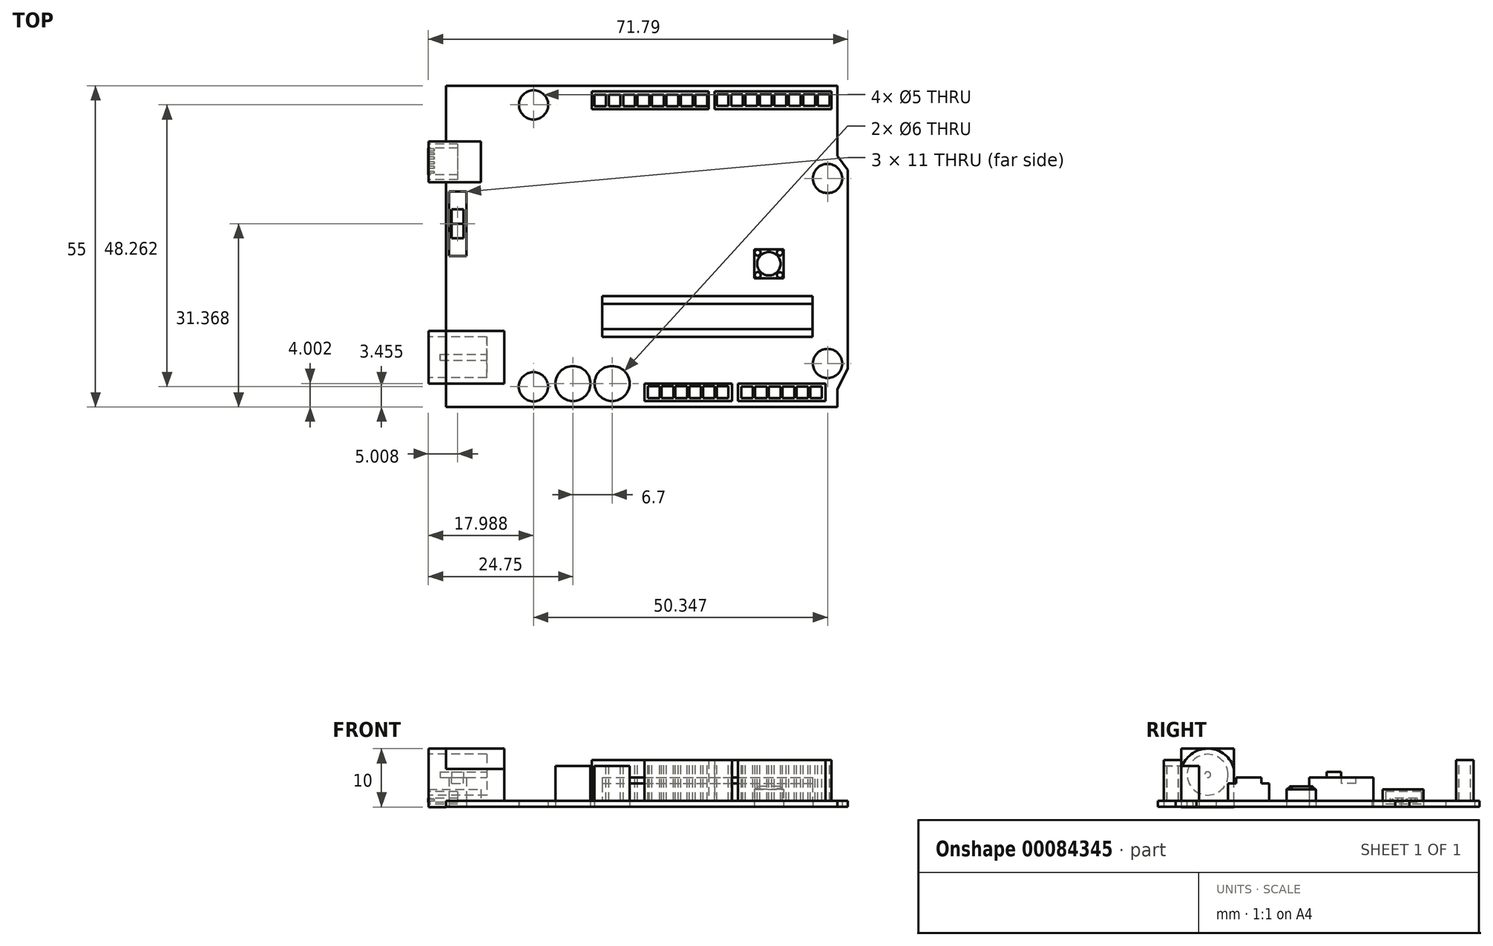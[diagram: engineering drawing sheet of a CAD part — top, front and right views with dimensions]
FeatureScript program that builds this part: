
annotation { "Feature Type Name" : "Feature", "Feature Type Description" : "" }
export const myFeature = defineFeature(function(context is Context, id is Id, definition is map)
    precondition{}
    {
        {
            var Q0;
            Q0=qCreatedBy(makeId("Top.planeOp"),FACE);
            var sketch = newSketch(context, id + "F0", { "sketchPlane" : qUnion([Q0])});
            skLineSegment(sketch, "E0.bottom", {"start": v(-37.2, 39.45) * mm, "end": v(29.8, 39.45) * mm});
            skLineSegment(sketch, "E0.top", {"start": v(-37.2, -15.55) * mm, "end": v(29.8, -15.55) * mm});
            skLineSegment(sketch, "E0.left", {"start": v(-37.2, 39.45) * mm, "end": v(-37.2, -15.55) * mm});
            skLineSegment(sketch, "E0.right", {"start": v(29.8, 39.45) * mm, "end": v(29.8, -15.55) * mm});
            skLineSegment(sketch, "E1", {"start": v(29.8, -12.55) * mm, "end": v(31.59, -8.97) * mm});
            skLineSegment(sketch, "E2", {"start": v(31.59, -8.97) * mm, "end": v(31.59, 25.03) * mm});
            skLineSegment(sketch, "E3", {"start": v(31.59, 25.03) * mm, "end": v(29.8, 27.45) * mm});
            skCircle(sketch, "E4", {"center": v(28.14, -8.11) * mm, "radius": 2.5 * mm});
            skCircle(sketch, "E5", {"center": v(-22.2, 36.17) * mm, "radius": 2.5 * mm});
            skCircle(sketch, "E6", {"center": v(28.14, 23.56) * mm, "radius": 2.5 * mm});
            skLineSegment(sketch, "E7", {"start": v(-22.2, 36.17) * mm, "end": v(-22.2, -14.2) * mm, "construction": true});
            skLineSegment(sketch, "E8", {"start": v(28.14, 23.56) * mm, "end": v(28.14, -13.38) * mm, "construction": true});
            skLineSegment(sketch, "E9.bottom", {"start": v(-40.2, 29.9) * mm, "end": v(-31.2, 29.9) * mm});
            skLineSegment(sketch, "E9.top", {"start": v(-40.2, 22.9) * mm, "end": v(-31.2, 22.9) * mm});
            skLineSegment(sketch, "E9.left", {"start": v(-40.2, 29.9) * mm, "end": v(-40.2, 22.9) * mm});
            skLineSegment(sketch, "E9.right", {"start": v(-31.2, 29.9) * mm, "end": v(-31.2, 22.9) * mm});
            skCircle(sketch, "E10", {"center": v(-22.21, -12.1) * mm, "radius": 2.5 * mm});
            skLineSegment(sketch, "E11.bottom", {"start": v(-3.2, -11.55) * mm, "end": v(11.8, -11.55) * mm});
            skLineSegment(sketch, "E11.top", {"start": v(-3.2, -14.55) * mm, "end": v(11.8, -14.55) * mm});
            skLineSegment(sketch, "E11.left", {"start": v(-3.2, -11.55) * mm, "end": v(-3.2, -14.55) * mm});
            skLineSegment(sketch, "E11.right", {"start": v(11.8, -11.55) * mm, "end": v(11.8, -14.55) * mm});
            skLineSegment(sketch, "E12.bottom", {"start": v(12.8, -11.55) * mm, "end": v(27.8, -11.55) * mm});
            skLineSegment(sketch, "E12.top", {"start": v(12.8, -14.55) * mm, "end": v(27.8, -14.55) * mm});
            skLineSegment(sketch, "E12.left", {"start": v(12.8, -11.55) * mm, "end": v(12.8, -14.55) * mm});
            skLineSegment(sketch, "E12.right", {"start": v(27.8, -11.55) * mm, "end": v(27.8, -14.55) * mm});
            skLineSegment(sketch, "E13.bottom", {"start": v(-12.2, 38.45) * mm, "end": v(7.8, 38.45) * mm});
            skLineSegment(sketch, "E13.top", {"start": v(-12.2, 35.45) * mm, "end": v(7.8, 35.45) * mm});
            skLineSegment(sketch, "E13.left", {"start": v(-12.2, 38.45) * mm, "end": v(-12.2, 35.45) * mm});
            skLineSegment(sketch, "E13.right", {"start": v(7.8, 38.45) * mm, "end": v(7.8, 35.45) * mm});
            skLineSegment(sketch, "E14.bottom", {"start": v(8.8, 38.45) * mm, "end": v(28.8, 38.45) * mm});
            skLineSegment(sketch, "E14.top", {"start": v(8.8, 35.45) * mm, "end": v(28.8, 35.45) * mm});
            skLineSegment(sketch, "E14.left", {"start": v(8.8, 38.45) * mm, "end": v(8.8, 35.45) * mm});
            skLineSegment(sketch, "E14.right", {"start": v(28.8, 38.45) * mm, "end": v(28.8, 35.45) * mm});
            skLineSegment(sketch, "E15.bottom", {"start": v(-10.41, 3.45) * mm, "end": v(25.59, 3.45) * mm});
            skLineSegment(sketch, "E15.top", {"start": v(-10.41, -3.55) * mm, "end": v(25.59, -3.55) * mm});
            skLineSegment(sketch, "E15.left", {"start": v(-10.41, 3.45) * mm, "end": v(-10.41, -3.55) * mm});
            skLineSegment(sketch, "E15.right", {"start": v(25.59, 3.45) * mm, "end": v(25.59, -3.55) * mm});
            skCircle(sketch, "E16", {"center": v(-8.75, -11.55) * mm, "radius": 3 * mm});
            skCircle(sketch, "E17", {"center": v(-15.45, -11.55) * mm, "radius": 3 * mm});
            skLineSegment(sketch, "E18", {"start": v(-3.2, -14.55) * mm, "end": v(-23.42, -14.6) * mm, "construction": true});
            skLineSegment(sketch, "E19.bottom", {"start": v(-36.7, 21.32) * mm, "end": v(-33.7, 21.32) * mm});
            skLineSegment(sketch, "E19.top", {"start": v(-36.7, 10.32) * mm, "end": v(-33.7, 10.32) * mm});
            skLineSegment(sketch, "E19.left", {"start": v(-36.7, 21.32) * mm, "end": v(-36.7, 10.32) * mm});
            skLineSegment(sketch, "E19.right", {"start": v(-33.7, 21.32) * mm, "end": v(-33.7, 10.32) * mm});
            skLineSegment(sketch, "E20.bottom", {"start": v(15.59, 11.45) * mm, "end": v(20.59, 11.45) * mm});
            skLineSegment(sketch, "E20.top", {"start": v(15.59, 6.45) * mm, "end": v(20.59, 6.45) * mm});
            skLineSegment(sketch, "E20.left", {"start": v(15.59, 11.45) * mm, "end": v(15.59, 6.45) * mm});
            skLineSegment(sketch, "E20.right", {"start": v(20.59, 11.45) * mm, "end": v(20.59, 6.45) * mm});
            skSolve(sketch);
        }
        {
            var Q0;
            {var subQ11=sQuery(id+"F0.wireOp",EDGE,"E0.bottom");Q0=makeQuery(id+"F0.imprint","IMPRINT",FACE,{"disambiguationData":[TD([[makeQuery(id+"F0.imprint","IMPRINT",EDGE,{"derivedFrom":subQ11}),-1.0]])]});}
            var Q1;
            {var subQ0=sQuery(id+"F0.wireOp",EDGE,"E1");Q1=makeQuery(id+"F0.imprint","IMPRINT",FACE,{"disambiguationData":[TD([[makeQuery(id+"F0.imprint","IMPRINT",EDGE,{"derivedFrom":subQ0}),1.0]])]});}
            extrude(context, id + "F1", {"entities" : qUnion([Q0, Q1]), "depth" : 1 * mm});
        }
        {
            var Q0;
            {var subQ5=sQuery(id+"F0.wireOp",EDGE,"E9.right");Q0=makeQuery(id+"F0.imprint","IMPRINT",FACE,{"disambiguationData":[TD([[makeQuery(id+"F0.imprint","IMPRINT",EDGE,{"derivedFrom":subQ5}),-1.0]])]});}
            var Q1;
            {var subQ5=sQuery(id+"F0.wireOp",EDGE,"E9.left");Q1=makeQuery(id+"F0.imprint","IMPRINT",FACE,{"disambiguationData":[TD([[makeQuery(id+"F0.imprint","IMPRINT",EDGE,{"derivedFrom":subQ5}),1.0]])]});}
            extrude(context, id + "F2", {"entities" : qUnion([Q0, Q1]), "operationType" : NewBodyOperationType.ADD, "depth" : 3 * mm});
        }
        {
            var Q0;
            Q0=makeQuery(id+"F2.opExtrude","SWEPT_FACE",FACE,{"disambiguationData":[OSD([sQuery(id+"F0.wireOp",EDGE,"E9.left")])]});
            var sketch = newSketch(context, id + "F3", { "sketchPlane" : qUnion([Q0])});
            skLineSegment(sketch, "E21.bottom", {"start": v(-29.48, 2.58) * mm, "end": v(-23.4, 2.58) * mm});
            skLineSegment(sketch, "E21.top", {"start": v(-29.48, 0.43) * mm, "end": v(-23.4, 0.43) * mm});
            skLineSegment(sketch, "E21.left", {"start": v(-29.48, 2.58) * mm, "end": v(-29.48, 0.43) * mm});
            skLineSegment(sketch, "E21.right", {"start": v(-23.4, 2.58) * mm, "end": v(-23.4, 0.43) * mm});
            skLineSegment(sketch, "E22.bottom", {"start": v(-28.8, 1.47) * mm, "end": v(-24.19, 1.47) * mm});
            skLineSegment(sketch, "E22.top", {"start": v(-28.8, 0.77) * mm, "end": v(-24.19, 0.77) * mm});
            skLineSegment(sketch, "E22.left", {"start": v(-28.8, 1.47) * mm, "end": v(-28.8, 0.77) * mm});
            skLineSegment(sketch, "E22.right", {"start": v(-24.19, 1.47) * mm, "end": v(-24.19, 0.77) * mm});
            skSolve(sketch);
        }
        {
            var Q0;
            Q0=makeQuery(id+"F3.imprint","IMPRINT",FACE,{"disambiguationData":[TD([[makeQuery(id+"F3.imprint","IMPRINT",EDGE,{"derivedFrom":sQuery(id+"F3.wireOp",EDGE,"E21.bottom")}),-1.0]])]});
            extrude(context, id + "F4", {"entities" : qUnion([Q0]), "operationType" : NewBodyOperationType.REMOVE, "oppositeDirection" : true, "depth" : 5 * mm});
        }
        {
            var Q0;
            Q0=makeQuery(id+"F4.boolean.opBoolean","SPLIT",FACE,{"disambiguationData":[TD([makeQuery(id+"F4.opExtrude","SWEPT_FACE",FACE,{"disambiguationData":[OSD([sQuery(id+"F3.wireOp",EDGE,"E22.bottom")])]})])],"derivedFrom":makeQuery(id+"F2.opExtrude","SWEPT_FACE",FACE,{"disambiguationData":[OSD([sQuery(id+"F0.wireOp",EDGE,"E9.left")])]})});
            extrude(context, id + "F5", {"entities" : qUnion([Q0]), "operationType" : NewBodyOperationType.ADD, "depth" : 0.01 * mm});
        }
        {
            var Q0;
            Q0=makeQuery(id+"F5.opExtrude","CAP_FACE",FACE,{"disambiguationData":[OSD([sQuery(id+"F0.wireOp",EDGE,"E9.left")])],"isStart":false});
            var sketch = newSketch(context, id + "F6", { "sketchPlane" : qUnion([Q0])});
            skCircle(sketch, "E23", {"center": v(-28.44, 1.13) * mm, "radius": 0.18 * mm});
            skCircle(sketch, "E24", {"center": v(-27.77, 1.13) * mm, "radius": 0.18 * mm});
            skCircle(sketch, "E25", {"center": v(-24.6, 1.13) * mm, "radius": 0.18 * mm});
            skCircle(sketch, "E26", {"center": v(-27.04, 1.14) * mm, "radius": 0.18 * mm});
            skCircle(sketch, "E27", {"center": v(-26.24, 1.13) * mm, "radius": 0.18 * mm});
            skCircle(sketch, "E28", {"center": v(-25.45, 1.13) * mm, "radius": 0.18 * mm});
            skSolve(sketch);
        }
        {
            var Q0;
            Q0=makeQuery(id+"F6.imprint","IMPRINT",FACE,{"disambiguationData":[TD([[makeQuery(id+"F6.imprint","IMPRINT",EDGE,{"derivedFrom":sQuery(id+"F6.wireOp",EDGE,"E23")}),1.0]])]});
            var Q1;
            Q1=makeQuery(id+"F6.imprint","IMPRINT",FACE,{"disambiguationData":[TD([[makeQuery(id+"F6.imprint","IMPRINT",EDGE,{"derivedFrom":sQuery(id+"F6.wireOp",EDGE,"E24")}),1.0]])]});
            var Q2;
            Q2=makeQuery(id+"F6.imprint","IMPRINT",FACE,{"disambiguationData":[TD([[makeQuery(id+"F6.imprint","IMPRINT",EDGE,{"derivedFrom":sQuery(id+"F6.wireOp",EDGE,"E26")}),1.0]])]});
            var Q3;
            Q3=makeQuery(id+"F6.imprint","IMPRINT",FACE,{"disambiguationData":[TD([[makeQuery(id+"F6.imprint","IMPRINT",EDGE,{"derivedFrom":sQuery(id+"F6.wireOp",EDGE,"E27")}),1.0]])]});
            var Q4;
            Q4=makeQuery(id+"F6.imprint","IMPRINT",FACE,{"disambiguationData":[TD([[makeQuery(id+"F6.imprint","IMPRINT",EDGE,{"derivedFrom":sQuery(id+"F6.wireOp",EDGE,"E28")}),1.0]])]});
            var Q5;
            Q5=makeQuery(id+"F6.imprint","IMPRINT",FACE,{"disambiguationData":[TD([[makeQuery(id+"F6.imprint","IMPRINT",EDGE,{"derivedFrom":sQuery(id+"F6.wireOp",EDGE,"E25")}),1.0]])]});
            var Q6;
            Q6=sQuery(id+"F6.wireOp",EDGE,"E23");
            var Q7;
            Q7=sQuery(id+"F6.wireOp",EDGE,"E24");
            var Q8;
            Q8=sQuery(id+"F6.wireOp",EDGE,"E26");
            var Q9;
            Q9=sQuery(id+"F6.wireOp",EDGE,"E27");
            var Q10;
            Q10=sQuery(id+"F6.wireOp",EDGE,"E28");
            var Q11;
            Q11=sQuery(id+"F6.wireOp",EDGE,"E25");
            extrude(context, id + "F7", {"entities" : qUnion([Q0, Q1, Q2, Q3, Q4, Q5]), "operationType" : NewBodyOperationType.REMOVE, "surfaceEntities" : qUnion([Q6, Q7, Q8, Q9, Q10, Q11]), "oppositeDirection" : true, "depth" : 1 * mm});
        }
        {
            var Q0;
            Q0=makeQuery(id+"F0.imprint","IMPRINT",FACE,{"disambiguationData":[TD([[makeQuery(id+"F0.imprint","IMPRINT",EDGE,{"derivedFrom":sQuery(id+"F0.wireOp",EDGE,"E11.bottom")}),-1.0]])]});
            var Q1;
            Q1=makeQuery(id+"F0.imprint","IMPRINT",FACE,{"disambiguationData":[TD([[makeQuery(id+"F0.imprint","IMPRINT",EDGE,{"derivedFrom":sQuery(id+"F0.wireOp",EDGE,"E12.bottom")}),-1.0]])]});
            extrude(context, id + "F8", {"entities" : qUnion([Q0, Q1]), "operationType" : NewBodyOperationType.ADD, "depth" : 8 * mm});
        }
        {
            var Q0;
            Q0=makeQuery(id+"F8.opExtrude","CAP_FACE",FACE,{"disambiguationData":[OSD([sQuery(id+"F0.wireOp",EDGE,"E11.bottom"),sQuery(id+"F0.wireOp",EDGE,"E11.top"),sQuery(id+"F0.wireOp",EDGE,"E11.left"),sQuery(id+"F0.wireOp",EDGE,"E11.right")])],"isStart":false});
            var sketch = newSketch(context, id + "F9", { "sketchPlane" : qUnion([Q0])});
            skLineSegment(sketch, "E29.bottom", {"start": v(-2.63, -12.01) * mm, "end": v(-0.63, -12.01) * mm});
            skLineSegment(sketch, "E29.top", {"start": v(-2.63, -14.01) * mm, "end": v(-0.63, -14.01) * mm});
            skLineSegment(sketch, "E29.left", {"start": v(-2.63, -12.01) * mm, "end": v(-2.63, -14.01) * mm});
            skLineSegment(sketch, "E29.right", {"start": v(-0.63, -12.01) * mm, "end": v(-0.63, -14.01) * mm});
            skLineSegment(sketch, "E30.1.0.0", {"start": v(-0.27, -12.01) * mm, "end": v(1.73, -12.01) * mm});
            skLineSegment(sketch, "E30.1.0.1", {"start": v(1.73, -12.01) * mm, "end": v(1.73, -14.01) * mm});
            skLineSegment(sketch, "E30.1.0.2", {"start": v(-0.27, -12.01) * mm, "end": v(-0.27, -14.01) * mm});
            skLineSegment(sketch, "E30.1.0.3", {"start": v(-0.27, -14.01) * mm, "end": v(1.73, -14.01) * mm});
            skLineSegment(sketch, "E30.2.0.0", {"start": v(2.1, -12.01) * mm, "end": v(4.1, -12.01) * mm});
            skLineSegment(sketch, "E30.2.0.1", {"start": v(4.1, -12.01) * mm, "end": v(4.1, -14.01) * mm});
            skLineSegment(sketch, "E30.2.0.2", {"start": v(2.1, -12.01) * mm, "end": v(2.1, -14.01) * mm});
            skLineSegment(sketch, "E30.2.0.3", {"start": v(2.1, -14.01) * mm, "end": v(4.1, -14.01) * mm});
            skLineSegment(sketch, "E30.3.0.0", {"start": v(4.45, -12.01) * mm, "end": v(6.45, -12.01) * mm});
            skLineSegment(sketch, "E30.3.0.1", {"start": v(6.45, -12.01) * mm, "end": v(6.45, -14.01) * mm});
            skLineSegment(sketch, "E30.3.0.2", {"start": v(4.45, -12.01) * mm, "end": v(4.45, -14.01) * mm});
            skLineSegment(sketch, "E30.3.0.3", {"start": v(4.45, -14.01) * mm, "end": v(6.45, -14.01) * mm});
            skLineSegment(sketch, "E30.4.0.0", {"start": v(6.8, -12.01) * mm, "end": v(8.8, -12.01) * mm});
            skLineSegment(sketch, "E30.4.0.1", {"start": v(8.8, -12.01) * mm, "end": v(8.8, -14.01) * mm});
            skLineSegment(sketch, "E30.4.0.2", {"start": v(6.8, -12.01) * mm, "end": v(6.8, -14.01) * mm});
            skLineSegment(sketch, "E30.4.0.3", {"start": v(6.8, -14.01) * mm, "end": v(8.8, -14.01) * mm});
            skLineSegment(sketch, "E30.5.0.0", {"start": v(9.17, -12.01) * mm, "end": v(11.17, -12.01) * mm});
            skLineSegment(sketch, "E30.5.0.1", {"start": v(11.17, -12.01) * mm, "end": v(11.17, -14.01) * mm});
            skLineSegment(sketch, "E30.5.0.2", {"start": v(9.17, -12.01) * mm, "end": v(9.17, -14.01) * mm});
            skLineSegment(sketch, "E30.5.0.3", {"start": v(9.17, -14.01) * mm, "end": v(11.17, -14.01) * mm});
            skLineSegment(sketch, "E30.direction1", {"start": v(-2.63, -12.01) * mm, "end": v(-0.27, -12.01) * mm, "construction": true});
            skLineSegment(sketch, "E31.bottom", {"start": v(13.37, -12.06) * mm, "end": v(15.37, -12.06) * mm});
            skLineSegment(sketch, "E31.top", {"start": v(13.37, -14.06) * mm, "end": v(15.37, -14.06) * mm});
            skLineSegment(sketch, "E31.left", {"start": v(13.37, -12.06) * mm, "end": v(13.37, -14.06) * mm});
            skLineSegment(sketch, "E31.right", {"start": v(15.37, -12.06) * mm, "end": v(15.37, -14.06) * mm});
            skLineSegment(sketch, "E32.1.0.0", {"start": v(15.73, -12.06) * mm, "end": v(17.73, -12.06) * mm});
            skLineSegment(sketch, "E32.1.0.1", {"start": v(17.73, -12.06) * mm, "end": v(17.73, -14.06) * mm});
            skLineSegment(sketch, "E32.1.0.2", {"start": v(15.73, -12.06) * mm, "end": v(15.73, -14.06) * mm});
            skLineSegment(sketch, "E32.1.0.3", {"start": v(15.73, -14.06) * mm, "end": v(17.73, -14.06) * mm});
            skLineSegment(sketch, "E32.2.0.0", {"start": v(18.09, -12.06) * mm, "end": v(20.09, -12.06) * mm});
            skLineSegment(sketch, "E32.2.0.1", {"start": v(20.09, -12.06) * mm, "end": v(20.09, -14.06) * mm});
            skLineSegment(sketch, "E32.2.0.2", {"start": v(18.09, -12.06) * mm, "end": v(18.09, -14.06) * mm});
            skLineSegment(sketch, "E32.2.0.3", {"start": v(18.09, -14.06) * mm, "end": v(20.09, -14.06) * mm});
            skLineSegment(sketch, "E32.3.0.0", {"start": v(20.45, -12.06) * mm, "end": v(22.45, -12.06) * mm});
            skLineSegment(sketch, "E32.3.0.1", {"start": v(22.45, -12.06) * mm, "end": v(22.45, -14.06) * mm});
            skLineSegment(sketch, "E32.3.0.2", {"start": v(20.45, -12.06) * mm, "end": v(20.45, -14.06) * mm});
            skLineSegment(sketch, "E32.3.0.3", {"start": v(20.45, -14.06) * mm, "end": v(22.45, -14.06) * mm});
            skLineSegment(sketch, "E32.4.0.0", {"start": v(22.8, -12.06) * mm, "end": v(24.8, -12.06) * mm});
            skLineSegment(sketch, "E32.4.0.1", {"start": v(24.8, -12.06) * mm, "end": v(24.8, -14.06) * mm});
            skLineSegment(sketch, "E32.4.0.2", {"start": v(22.8, -12.06) * mm, "end": v(22.8, -14.06) * mm});
            skLineSegment(sketch, "E32.4.0.3", {"start": v(22.8, -14.06) * mm, "end": v(24.8, -14.06) * mm});
            skLineSegment(sketch, "E32.5.0.0", {"start": v(25.16, -12.06) * mm, "end": v(27.16, -12.06) * mm});
            skLineSegment(sketch, "E32.5.0.1", {"start": v(27.16, -12.06) * mm, "end": v(27.16, -14.06) * mm});
            skLineSegment(sketch, "E32.5.0.2", {"start": v(25.16, -12.06) * mm, "end": v(25.16, -14.06) * mm});
            skLineSegment(sketch, "E32.5.0.3", {"start": v(25.16, -14.06) * mm, "end": v(27.16, -14.06) * mm});
            skLineSegment(sketch, "E32.direction1", {"start": v(13.37, -12.06) * mm, "end": v(15.73, -12.06) * mm, "construction": true});
            skSolve(sketch);
        }
        {
            var Q0;
            Q0=makeQuery(id+"F9.imprint","IMPRINT",FACE,{"disambiguationData":[TD([[makeQuery(id+"F9.imprint","IMPRINT",EDGE,{"derivedFrom":sQuery(id+"F9.wireOp",EDGE,"E29.bottom")}),-1.0]])]});
            var Q1;
            Q1=makeQuery(id+"F9.imprint","IMPRINT",FACE,{"disambiguationData":[TD([[makeQuery(id+"F9.imprint","IMPRINT",EDGE,{"derivedFrom":sQuery(id+"F9.wireOp",EDGE,"E30.1.0.0")}),-1.0]])]});
            var Q2;
            Q2=makeQuery(id+"F9.imprint","IMPRINT",FACE,{"disambiguationData":[TD([[makeQuery(id+"F9.imprint","IMPRINT",EDGE,{"derivedFrom":sQuery(id+"F9.wireOp",EDGE,"E30.2.0.0")}),-1.0]])]});
            var Q3;
            Q3=makeQuery(id+"F9.imprint","IMPRINT",FACE,{"disambiguationData":[TD([[makeQuery(id+"F9.imprint","IMPRINT",EDGE,{"derivedFrom":sQuery(id+"F9.wireOp",EDGE,"E30.3.0.0")}),-1.0]])]});
            var Q4;
            Q4=makeQuery(id+"F9.imprint","IMPRINT",FACE,{"disambiguationData":[TD([[makeQuery(id+"F9.imprint","IMPRINT",EDGE,{"derivedFrom":sQuery(id+"F9.wireOp",EDGE,"E30.4.0.0")}),-1.0]])]});
            var Q5;
            Q5=makeQuery(id+"F9.imprint","IMPRINT",FACE,{"disambiguationData":[TD([[makeQuery(id+"F9.imprint","IMPRINT",EDGE,{"derivedFrom":sQuery(id+"F9.wireOp",EDGE,"E30.5.0.0")}),-1.0]])]});
            var Q6;
            Q6=makeQuery(id+"F9.imprint","IMPRINT",FACE,{"disambiguationData":[TD([[makeQuery(id+"F9.imprint","IMPRINT",EDGE,{"derivedFrom":sQuery(id+"F9.wireOp",EDGE,"E31.bottom")}),-1.0]])]});
            var Q7;
            Q7=makeQuery(id+"F9.imprint","IMPRINT",FACE,{"disambiguationData":[TD([[makeQuery(id+"F9.imprint","IMPRINT",EDGE,{"derivedFrom":sQuery(id+"F9.wireOp",EDGE,"E32.1.0.0")}),-1.0]])]});
            var Q8;
            Q8=makeQuery(id+"F9.imprint","IMPRINT",FACE,{"disambiguationData":[TD([[makeQuery(id+"F9.imprint","IMPRINT",EDGE,{"derivedFrom":sQuery(id+"F9.wireOp",EDGE,"E32.2.0.0")}),-1.0]])]});
            var Q9;
            Q9=makeQuery(id+"F9.imprint","IMPRINT",FACE,{"disambiguationData":[TD([[makeQuery(id+"F9.imprint","IMPRINT",EDGE,{"derivedFrom":sQuery(id+"F9.wireOp",EDGE,"E32.3.0.0")}),-1.0]])]});
            var Q10;
            Q10=makeQuery(id+"F9.imprint","IMPRINT",FACE,{"disambiguationData":[TD([[makeQuery(id+"F9.imprint","IMPRINT",EDGE,{"derivedFrom":sQuery(id+"F9.wireOp",EDGE,"E32.4.0.0")}),-1.0]])]});
            var Q11;
            Q11=makeQuery(id+"F9.imprint","IMPRINT",FACE,{"disambiguationData":[TD([[makeQuery(id+"F9.imprint","IMPRINT",EDGE,{"derivedFrom":sQuery(id+"F9.wireOp",EDGE,"E32.5.0.0")}),-1.0]])]});
            var Q12;
            Q12=sQuery(id+"F9.wireOp",EDGE,"e2aa6071-b982-4bc8-af80-e95c8fd193ff.bottom");
            var Q13;
            Q13=sQuery(id+"F9.wireOp",EDGE,"e2aa6071-b982-4bc8-af80-e95c8fd193ff.top");
            var Q14;
            Q14=sQuery(id+"F9.wireOp",EDGE,"e2aa6071-b982-4bc8-af80-e95c8fd193ff.left");
            var Q15;
            Q15=sQuery(id+"F9.wireOp",EDGE,"e2aa6071-b982-4bc8-af80-e95c8fd193ff.right");
            var Q16;
            Q16=sQuery(id+"F9.wireOp",EDGE,"8d807763-f77d-4302-8a10-7eaa0a08b874.1.0.0");
            var Q17;
            Q17=sQuery(id+"F9.wireOp",EDGE,"8d807763-f77d-4302-8a10-7eaa0a08b874.1.0.1");
            var Q18;
            Q18=sQuery(id+"F9.wireOp",EDGE,"8d807763-f77d-4302-8a10-7eaa0a08b874.1.0.2");
            var Q19;
            Q19=sQuery(id+"F9.wireOp",EDGE,"8d807763-f77d-4302-8a10-7eaa0a08b874.1.0.3");
            var Q20;
            Q20=sQuery(id+"F9.wireOp",EDGE,"8d807763-f77d-4302-8a10-7eaa0a08b874.2.0.0");
            var Q21;
            Q21=sQuery(id+"F9.wireOp",EDGE,"8d807763-f77d-4302-8a10-7eaa0a08b874.2.0.1");
            var Q22;
            Q22=sQuery(id+"F9.wireOp",EDGE,"8d807763-f77d-4302-8a10-7eaa0a08b874.2.0.2");
            var Q23;
            Q23=sQuery(id+"F9.wireOp",EDGE,"8d807763-f77d-4302-8a10-7eaa0a08b874.2.0.3");
            var Q24;
            Q24=sQuery(id+"F9.wireOp",EDGE,"8d807763-f77d-4302-8a10-7eaa0a08b874.3.0.0");
            var Q25;
            Q25=sQuery(id+"F9.wireOp",EDGE,"8d807763-f77d-4302-8a10-7eaa0a08b874.3.0.1");
            var Q26;
            Q26=sQuery(id+"F9.wireOp",EDGE,"8d807763-f77d-4302-8a10-7eaa0a08b874.3.0.2");
            var Q27;
            Q27=sQuery(id+"F9.wireOp",EDGE,"8d807763-f77d-4302-8a10-7eaa0a08b874.3.0.3");
            var Q28;
            Q28=sQuery(id+"F9.wireOp",EDGE,"8d807763-f77d-4302-8a10-7eaa0a08b874.4.0.0");
            var Q29;
            Q29=sQuery(id+"F9.wireOp",EDGE,"8d807763-f77d-4302-8a10-7eaa0a08b874.4.0.1");
            var Q30;
            Q30=sQuery(id+"F9.wireOp",EDGE,"8d807763-f77d-4302-8a10-7eaa0a08b874.4.0.2");
            var Q31;
            Q31=sQuery(id+"F9.wireOp",EDGE,"8d807763-f77d-4302-8a10-7eaa0a08b874.4.0.3");
            var Q32;
            Q32=sQuery(id+"F9.wireOp",EDGE,"8d807763-f77d-4302-8a10-7eaa0a08b874.5.0.0");
            var Q33;
            Q33=sQuery(id+"F9.wireOp",EDGE,"8d807763-f77d-4302-8a10-7eaa0a08b874.5.0.1");
            var Q34;
            Q34=sQuery(id+"F9.wireOp",EDGE,"8d807763-f77d-4302-8a10-7eaa0a08b874.5.0.2");
            var Q35;
            Q35=sQuery(id+"F9.wireOp",EDGE,"8d807763-f77d-4302-8a10-7eaa0a08b874.5.0.3");
            extrude(context, id + "F10", {"entities" : qUnion([Q0, Q1, Q2, Q3, Q4, Q5, Q6, Q7, Q8, Q9, Q10, Q11]), "operationType" : NewBodyOperationType.REMOVE, "surfaceEntities" : qUnion([Q12, Q13, Q14, Q15, Q16, Q17, Q18, Q19, Q20, Q21, Q22, Q23, Q24, Q25, Q26, Q27, Q28, Q29, Q30, Q31, Q32, Q33, Q34, Q35]), "oppositeDirection" : true, "depth" : 7 * mm});
        }
        {
            var Q0;
            Q0=makeQuery(id+"F0.imprint","IMPRINT",FACE,{"disambiguationData":[TD([[makeQuery(id+"F0.imprint","IMPRINT",EDGE,{"derivedFrom":sQuery(id+"F0.wireOp",EDGE,"E13.bottom")}),-1.0]])]});
            var Q1;
            Q1=makeQuery(id+"F0.imprint","IMPRINT",FACE,{"disambiguationData":[TD([[makeQuery(id+"F0.imprint","IMPRINT",EDGE,{"derivedFrom":sQuery(id+"F0.wireOp",EDGE,"E14.bottom")}),-1.0]])]});
            extrude(context, id + "F11", {"entities" : qUnion([Q0, Q1]), "operationType" : NewBodyOperationType.ADD, "depth" : 8 * mm});
        }
        {
            var Q0;
            Q0=makeQuery(id+"F11.opExtrude","CAP_FACE",FACE,{"disambiguationData":[OSD([sQuery(id+"F0.wireOp",EDGE,"E13.bottom"),sQuery(id+"F0.wireOp",EDGE,"E13.top"),sQuery(id+"F0.wireOp",EDGE,"E13.left"),sQuery(id+"F0.wireOp",EDGE,"E13.right")])],"isStart":false});
            var sketch = newSketch(context, id + "F12", { "sketchPlane" : qUnion([Q0])});
            skLineSegment(sketch, "E33.bottom", {"start": v(-11.8, 37.93) * mm, "end": v(-9.8, 37.93) * mm});
            skLineSegment(sketch, "E33.top", {"start": v(-11.8, 35.93) * mm, "end": v(-9.8, 35.93) * mm});
            skLineSegment(sketch, "E33.left", {"start": v(-11.8, 37.93) * mm, "end": v(-11.8, 35.93) * mm});
            skLineSegment(sketch, "E33.right", {"start": v(-9.8, 37.93) * mm, "end": v(-9.8, 35.93) * mm});
            skLineSegment(sketch, "E34.1.0.0", {"start": v(-9.32, 35.93) * mm, "end": v(-7.32, 35.93) * mm});
            skLineSegment(sketch, "E34.1.0.1", {"start": v(-9.32, 37.93) * mm, "end": v(-9.32, 35.93) * mm});
            skLineSegment(sketch, "E34.1.0.2", {"start": v(-7.32, 37.93) * mm, "end": v(-7.32, 35.93) * mm});
            skLineSegment(sketch, "E34.1.0.3", {"start": v(-9.32, 37.93) * mm, "end": v(-7.32, 37.93) * mm});
            skLineSegment(sketch, "E34.2.0.0", {"start": v(-6.85, 35.93) * mm, "end": v(-4.85, 35.93) * mm});
            skLineSegment(sketch, "E34.2.0.1", {"start": v(-6.85, 37.93) * mm, "end": v(-6.85, 35.93) * mm});
            skLineSegment(sketch, "E34.2.0.2", {"start": v(-4.85, 37.93) * mm, "end": v(-4.85, 35.93) * mm});
            skLineSegment(sketch, "E34.2.0.3", {"start": v(-6.85, 37.93) * mm, "end": v(-4.85, 37.93) * mm});
            skLineSegment(sketch, "E34.3.0.0", {"start": v(-4.38, 35.93) * mm, "end": v(-2.38, 35.93) * mm});
            skLineSegment(sketch, "E34.3.0.1", {"start": v(-4.38, 37.93) * mm, "end": v(-4.38, 35.93) * mm});
            skLineSegment(sketch, "E34.3.0.2", {"start": v(-2.38, 37.93) * mm, "end": v(-2.38, 35.93) * mm});
            skLineSegment(sketch, "E34.3.0.3", {"start": v(-4.38, 37.93) * mm, "end": v(-2.38, 37.93) * mm});
            skLineSegment(sketch, "E34.4.0.0", {"start": v(-1.9, 35.93) * mm, "end": v(0.1, 35.93) * mm});
            skLineSegment(sketch, "E34.4.0.1", {"start": v(-1.9, 37.93) * mm, "end": v(-1.9, 35.93) * mm});
            skLineSegment(sketch, "E34.4.0.2", {"start": v(0.1, 37.93) * mm, "end": v(0.1, 35.93) * mm});
            skLineSegment(sketch, "E34.4.0.3", {"start": v(-1.9, 37.93) * mm, "end": v(0.1, 37.93) * mm});
            skLineSegment(sketch, "E34.5.0.0", {"start": v(0.57, 35.93) * mm, "end": v(2.57, 35.93) * mm});
            skLineSegment(sketch, "E34.5.0.1", {"start": v(0.57, 37.93) * mm, "end": v(0.57, 35.93) * mm});
            skLineSegment(sketch, "E34.5.0.2", {"start": v(2.57, 37.93) * mm, "end": v(2.57, 35.93) * mm});
            skLineSegment(sketch, "E34.5.0.3", {"start": v(0.57, 37.93) * mm, "end": v(2.57, 37.93) * mm});
            skLineSegment(sketch, "E34.6.0.0", {"start": v(3.04, 35.93) * mm, "end": v(5.04, 35.93) * mm});
            skLineSegment(sketch, "E34.6.0.1", {"start": v(3.04, 37.93) * mm, "end": v(3.04, 35.93) * mm});
            skLineSegment(sketch, "E34.6.0.2", {"start": v(5.04, 37.93) * mm, "end": v(5.04, 35.93) * mm});
            skLineSegment(sketch, "E34.6.0.3", {"start": v(3.04, 37.93) * mm, "end": v(5.04, 37.93) * mm});
            skLineSegment(sketch, "E34.7.0.0", {"start": v(5.5, 35.93) * mm, "end": v(7.5, 35.93) * mm});
            skLineSegment(sketch, "E34.7.0.1", {"start": v(5.5, 37.93) * mm, "end": v(5.5, 35.93) * mm});
            skLineSegment(sketch, "E34.7.0.2", {"start": v(7.5, 37.93) * mm, "end": v(7.5, 35.93) * mm});
            skLineSegment(sketch, "E34.7.0.3", {"start": v(5.5, 37.93) * mm, "end": v(7.5, 37.93) * mm});
            skLineSegment(sketch, "E34.direction1", {"start": v(-11.8, 35.93) * mm, "end": v(-9.32, 35.93) * mm, "construction": true});
            skLineSegment(sketch, "E35.bottom", {"start": v(9.16, 37.98) * mm, "end": v(11.16, 37.98) * mm});
            skLineSegment(sketch, "E35.top", {"start": v(9.16, 35.98) * mm, "end": v(11.16, 35.98) * mm});
            skLineSegment(sketch, "E35.left", {"start": v(9.16, 37.98) * mm, "end": v(9.16, 35.98) * mm});
            skLineSegment(sketch, "E35.right", {"start": v(11.16, 37.98) * mm, "end": v(11.16, 35.98) * mm});
            skLineSegment(sketch, "E36.1.0.0", {"start": v(11.63, 35.98) * mm, "end": v(13.63, 35.98) * mm});
            skLineSegment(sketch, "E36.1.0.1", {"start": v(11.63, 37.98) * mm, "end": v(11.63, 35.98) * mm});
            skLineSegment(sketch, "E36.1.0.2", {"start": v(13.63, 37.98) * mm, "end": v(13.63, 35.98) * mm});
            skLineSegment(sketch, "E36.1.0.3", {"start": v(11.63, 37.98) * mm, "end": v(13.63, 37.98) * mm});
            skLineSegment(sketch, "E36.2.0.0", {"start": v(14.1, 35.98) * mm, "end": v(16.1, 35.98) * mm});
            skLineSegment(sketch, "E36.2.0.1", {"start": v(14.1, 37.98) * mm, "end": v(14.1, 35.98) * mm});
            skLineSegment(sketch, "E36.2.0.2", {"start": v(16.1, 37.98) * mm, "end": v(16.1, 35.98) * mm});
            skLineSegment(sketch, "E36.2.0.3", {"start": v(14.1, 37.98) * mm, "end": v(16.1, 37.98) * mm});
            skLineSegment(sketch, "E36.3.0.0", {"start": v(16.57, 35.98) * mm, "end": v(18.57, 35.98) * mm});
            skLineSegment(sketch, "E36.3.0.1", {"start": v(16.57, 37.98) * mm, "end": v(16.57, 35.98) * mm});
            skLineSegment(sketch, "E36.3.0.2", {"start": v(18.57, 37.98) * mm, "end": v(18.57, 35.98) * mm});
            skLineSegment(sketch, "E36.3.0.3", {"start": v(16.57, 37.98) * mm, "end": v(18.57, 37.98) * mm});
            skLineSegment(sketch, "E36.4.0.0", {"start": v(19.04, 35.98) * mm, "end": v(21.04, 35.98) * mm});
            skLineSegment(sketch, "E36.4.0.1", {"start": v(19.04, 37.98) * mm, "end": v(19.04, 35.98) * mm});
            skLineSegment(sketch, "E36.4.0.2", {"start": v(21.04, 37.98) * mm, "end": v(21.04, 35.98) * mm});
            skLineSegment(sketch, "E36.4.0.3", {"start": v(19.04, 37.98) * mm, "end": v(21.04, 37.98) * mm});
            skLineSegment(sketch, "E36.5.0.0", {"start": v(21.51, 35.98) * mm, "end": v(23.51, 35.98) * mm});
            skLineSegment(sketch, "E36.5.0.1", {"start": v(21.51, 37.98) * mm, "end": v(21.51, 35.98) * mm});
            skLineSegment(sketch, "E36.5.0.2", {"start": v(23.51, 37.98) * mm, "end": v(23.51, 35.98) * mm});
            skLineSegment(sketch, "E36.5.0.3", {"start": v(21.51, 37.98) * mm, "end": v(23.51, 37.98) * mm});
            skLineSegment(sketch, "E36.6.0.0", {"start": v(23.99, 35.98) * mm, "end": v(25.99, 35.98) * mm});
            skLineSegment(sketch, "E36.6.0.1", {"start": v(23.99, 37.98) * mm, "end": v(23.99, 35.98) * mm});
            skLineSegment(sketch, "E36.6.0.2", {"start": v(25.99, 37.98) * mm, "end": v(25.99, 35.98) * mm});
            skLineSegment(sketch, "E36.6.0.3", {"start": v(23.99, 37.98) * mm, "end": v(25.99, 37.98) * mm});
            skLineSegment(sketch, "E36.7.0.0", {"start": v(26.46, 35.98) * mm, "end": v(28.46, 35.98) * mm});
            skLineSegment(sketch, "E36.7.0.1", {"start": v(26.46, 37.98) * mm, "end": v(26.46, 35.98) * mm});
            skLineSegment(sketch, "E36.7.0.2", {"start": v(28.46, 37.98) * mm, "end": v(28.46, 35.98) * mm});
            skLineSegment(sketch, "E36.7.0.3", {"start": v(26.46, 37.98) * mm, "end": v(28.46, 37.98) * mm});
            skLineSegment(sketch, "E36.direction1", {"start": v(9.16, 35.98) * mm, "end": v(11.63, 35.98) * mm, "construction": true});
            skSolve(sketch);
        }
        {
            var Q0;
            Q0=makeQuery(id+"F12.imprint","IMPRINT",FACE,{"disambiguationData":[TD([[makeQuery(id+"F12.imprint","IMPRINT",EDGE,{"derivedFrom":sQuery(id+"F12.wireOp",EDGE,"E33.bottom")}),-1.0]])]});
            var Q1;
            Q1=makeQuery(id+"F12.imprint","IMPRINT",FACE,{"disambiguationData":[TD([[makeQuery(id+"F12.imprint","IMPRINT",EDGE,{"derivedFrom":sQuery(id+"F12.wireOp",EDGE,"E34.1.0.0")}),1.0]])]});
            var Q2;
            Q2=makeQuery(id+"F12.imprint","IMPRINT",FACE,{"disambiguationData":[TD([[makeQuery(id+"F12.imprint","IMPRINT",EDGE,{"derivedFrom":sQuery(id+"F12.wireOp",EDGE,"E34.2.0.0")}),1.0]])]});
            var Q3;
            Q3=makeQuery(id+"F12.imprint","IMPRINT",FACE,{"disambiguationData":[TD([[makeQuery(id+"F12.imprint","IMPRINT",EDGE,{"derivedFrom":sQuery(id+"F12.wireOp",EDGE,"E34.3.0.0")}),1.0]])]});
            var Q4;
            Q4=makeQuery(id+"F12.imprint","IMPRINT",FACE,{"disambiguationData":[TD([[makeQuery(id+"F12.imprint","IMPRINT",EDGE,{"derivedFrom":sQuery(id+"F12.wireOp",EDGE,"E34.7.0.0")}),1.0]])]});
            var Q5;
            Q5=makeQuery(id+"F12.imprint","IMPRINT",FACE,{"disambiguationData":[TD([[makeQuery(id+"F12.imprint","IMPRINT",EDGE,{"derivedFrom":sQuery(id+"F12.wireOp",EDGE,"E34.6.0.0")}),1.0]])]});
            var Q6;
            Q6=makeQuery(id+"F12.imprint","IMPRINT",FACE,{"disambiguationData":[TD([[makeQuery(id+"F12.imprint","IMPRINT",EDGE,{"derivedFrom":sQuery(id+"F12.wireOp",EDGE,"E34.5.0.0")}),1.0]])]});
            var Q7;
            Q7=makeQuery(id+"F12.imprint","IMPRINT",FACE,{"disambiguationData":[TD([[makeQuery(id+"F12.imprint","IMPRINT",EDGE,{"derivedFrom":sQuery(id+"F12.wireOp",EDGE,"E34.4.0.0")}),1.0]])]});
            var Q8;
            Q8=makeQuery(id+"F12.imprint","IMPRINT",FACE,{"disambiguationData":[TD([[makeQuery(id+"F12.imprint","IMPRINT",EDGE,{"derivedFrom":sQuery(id+"F12.wireOp",EDGE,"E35.bottom")}),-1.0]])]});
            var Q9;
            Q9=makeQuery(id+"F12.imprint","IMPRINT",FACE,{"disambiguationData":[TD([[makeQuery(id+"F12.imprint","IMPRINT",EDGE,{"derivedFrom":sQuery(id+"F12.wireOp",EDGE,"E36.1.0.0")}),1.0]])]});
            var Q10;
            Q10=makeQuery(id+"F12.imprint","IMPRINT",FACE,{"disambiguationData":[TD([[makeQuery(id+"F12.imprint","IMPRINT",EDGE,{"derivedFrom":sQuery(id+"F12.wireOp",EDGE,"E36.2.0.0")}),1.0]])]});
            var Q11;
            Q11=makeQuery(id+"F12.imprint","IMPRINT",FACE,{"disambiguationData":[TD([[makeQuery(id+"F12.imprint","IMPRINT",EDGE,{"derivedFrom":sQuery(id+"F12.wireOp",EDGE,"E36.3.0.0")}),1.0]])]});
            var Q12;
            Q12=makeQuery(id+"F12.imprint","IMPRINT",FACE,{"disambiguationData":[TD([[makeQuery(id+"F12.imprint","IMPRINT",EDGE,{"derivedFrom":sQuery(id+"F12.wireOp",EDGE,"E36.4.0.0")}),1.0]])]});
            var Q13;
            Q13=makeQuery(id+"F12.imprint","IMPRINT",FACE,{"disambiguationData":[TD([[makeQuery(id+"F12.imprint","IMPRINT",EDGE,{"derivedFrom":sQuery(id+"F12.wireOp",EDGE,"E36.5.0.0")}),1.0]])]});
            var Q14;
            Q14=makeQuery(id+"F12.imprint","IMPRINT",FACE,{"disambiguationData":[TD([[makeQuery(id+"F12.imprint","IMPRINT",EDGE,{"derivedFrom":sQuery(id+"F12.wireOp",EDGE,"E36.6.0.0")}),1.0]])]});
            var Q15;
            Q15=makeQuery(id+"F12.imprint","IMPRINT",FACE,{"disambiguationData":[TD([[makeQuery(id+"F12.imprint","IMPRINT",EDGE,{"derivedFrom":sQuery(id+"F12.wireOp",EDGE,"E36.7.0.0")}),1.0]])]});
            var Q16;
            Q16=sQuery(id+"F12.wireOp",EDGE,"E35.bottom");
            var Q17;
            Q17=sQuery(id+"F12.wireOp",EDGE,"E35.top");
            var Q18;
            Q18=sQuery(id+"F12.wireOp",EDGE,"E35.left");
            var Q19;
            Q19=sQuery(id+"F12.wireOp",EDGE,"E35.right");
            var Q20;
            Q20=sQuery(id+"F12.wireOp",EDGE,"E36.1.0.0");
            var Q21;
            Q21=sQuery(id+"F12.wireOp",EDGE,"E36.1.0.1");
            var Q22;
            Q22=sQuery(id+"F12.wireOp",EDGE,"E36.1.0.2");
            var Q23;
            Q23=sQuery(id+"F12.wireOp",EDGE,"E36.1.0.3");
            var Q24;
            Q24=sQuery(id+"F12.wireOp",EDGE,"E36.2.0.0");
            var Q25;
            Q25=sQuery(id+"F12.wireOp",EDGE,"E36.2.0.1");
            var Q26;
            Q26=sQuery(id+"F12.wireOp",EDGE,"E36.2.0.2");
            var Q27;
            Q27=sQuery(id+"F12.wireOp",EDGE,"E36.2.0.3");
            var Q28;
            Q28=sQuery(id+"F12.wireOp",EDGE,"E36.3.0.0");
            var Q29;
            Q29=sQuery(id+"F12.wireOp",EDGE,"E36.3.0.1");
            var Q30;
            Q30=sQuery(id+"F12.wireOp",EDGE,"E36.3.0.2");
            var Q31;
            Q31=sQuery(id+"F12.wireOp",EDGE,"E36.3.0.3");
            var Q32;
            Q32=sQuery(id+"F12.wireOp",EDGE,"E36.4.0.0");
            var Q33;
            Q33=sQuery(id+"F12.wireOp",EDGE,"E36.4.0.1");
            var Q34;
            Q34=sQuery(id+"F12.wireOp",EDGE,"E36.4.0.2");
            var Q35;
            Q35=sQuery(id+"F12.wireOp",EDGE,"E36.4.0.3");
            var Q36;
            Q36=sQuery(id+"F12.wireOp",EDGE,"E36.5.0.0");
            var Q37;
            Q37=sQuery(id+"F12.wireOp",EDGE,"E36.5.0.1");
            var Q38;
            Q38=sQuery(id+"F12.wireOp",EDGE,"E36.5.0.2");
            var Q39;
            Q39=sQuery(id+"F12.wireOp",EDGE,"E36.5.0.3");
            var Q40;
            Q40=sQuery(id+"F12.wireOp",EDGE,"E36.6.0.0");
            var Q41;
            Q41=sQuery(id+"F12.wireOp",EDGE,"E36.6.0.1");
            var Q42;
            Q42=sQuery(id+"F12.wireOp",EDGE,"E36.6.0.2");
            var Q43;
            Q43=sQuery(id+"F12.wireOp",EDGE,"E36.6.0.3");
            var Q44;
            Q44=sQuery(id+"F12.wireOp",EDGE,"E36.7.0.0");
            var Q45;
            Q45=sQuery(id+"F12.wireOp",EDGE,"E36.7.0.1");
            var Q46;
            Q46=sQuery(id+"F12.wireOp",EDGE,"E36.7.0.2");
            var Q47;
            Q47=sQuery(id+"F12.wireOp",EDGE,"E36.7.0.3");
            extrude(context, id + "F13", {"entities" : qUnion([Q0, Q1, Q2, Q3, Q4, Q5, Q6, Q7, Q8, Q9, Q10, Q11, Q12, Q13, Q14, Q15]), "operationType" : NewBodyOperationType.REMOVE, "surfaceEntities" : qUnion([Q16, Q17, Q18, Q19, Q20, Q21, Q22, Q23, Q24, Q25, Q26, Q27, Q28, Q29, Q30, Q31, Q32, Q33, Q34, Q35, Q36, Q37, Q38, Q39, Q40, Q41, Q42, Q43, Q44, Q45, Q46, Q47]), "oppositeDirection" : true, "depth" : 7 * mm});
        }
        {
            var Q0;
            Q0=makeQuery(id+"F0.imprint","IMPRINT",FACE,{"disambiguationData":[TD([[makeQuery(id+"F0.imprint","IMPRINT",EDGE,{"derivedFrom":sQuery(id+"F0.wireOp",EDGE,"E15.bottom")}),-1.0]])]});
            extrude(context, id + "F14", {"entities" : qUnion([Q0]), "operationType" : NewBodyOperationType.ADD, "depth" : 4 * mm});
        }
        {
            var Q0;
            Q0=makeQuery(id+"F14.opExtrude","CAP_FACE",FACE,{"disambiguationData":[OSD([sQuery(id+"F0.wireOp",EDGE,"E15.bottom"),sQuery(id+"F0.wireOp",EDGE,"E15.top"),sQuery(id+"F0.wireOp",EDGE,"E15.left"),sQuery(id+"F0.wireOp",EDGE,"E15.right")])],"isStart":false});
            var sketch = newSketch(context, id + "F15", { "sketchPlane" : qUnion([Q0])});
            skLineSegment(sketch, "E37.bottom", {"start": v(-10.41, 2.12) * mm, "end": v(25.59, 2.12) * mm});
            skLineSegment(sketch, "E37.top", {"start": v(-10.41, -2.2) * mm, "end": v(25.59, -2.2) * mm});
            skLineSegment(sketch, "E37.left", {"start": v(-10.41, 2.12) * mm, "end": v(-10.41, -2.2) * mm});
            skLineSegment(sketch, "E37.right", {"start": v(25.59, 2.12) * mm, "end": v(25.59, -2.2) * mm});
            skSolve(sketch);
        }
        {
            var Q0;
            Q0=makeQuery(id+"F15.imprint","IMPRINT",FACE,{"disambiguationData":[TD([[makeQuery(id+"F15.imprint","IMPRINT",EDGE,{"derivedFrom":sQuery(id+"F15.wireOp",EDGE,"E37.bottom")}),-1.0]])]});
            extrude(context, id + "F16", {"entities" : qUnion([Q0]), "operationType" : NewBodyOperationType.ADD, "depth" : 1 * mm});
        }
        {
            var Q0;
            Q0=makeQuery(id+"F0.imprint","IMPRINT",FACE,{"disambiguationData":[TD([[makeQuery(id+"F0.imprint","IMPRINT",EDGE,{"derivedFrom":sQuery(id+"F0.wireOp",EDGE,"E17")}),1.0]])]});
            var Q1;
            Q1=makeQuery(id+"F0.imprint","IMPRINT",FACE,{"disambiguationData":[TD([[makeQuery(id+"F0.imprint","IMPRINT",EDGE,{"derivedFrom":sQuery(id+"F0.wireOp",EDGE,"E16")}),1.0]])]});
            extrude(context, id + "F17", {"entities" : qUnion([Q0, Q1]), "depth" : 7 * mm});
        }
        {
            var Q0;
            Q0=makeQuery(id+"F0.imprint","IMPRINT",FACE,{"disambiguationData":[TD([[makeQuery(id+"F0.imprint","IMPRINT",EDGE,{"derivedFrom":sQuery(id+"F0.wireOp",EDGE,"E19.bottom")}),-1.0]])]});
            extrude(context, id + "F18", {"entities" : qUnion([Q0]), "depth" : 5 * mm});
        }
        {
            var Q0;
            Q0=makeQuery(id+"F18.opExtrude","CAP_FACE",FACE,{"disambiguationData":[OSD([sQuery(id+"F0.wireOp",EDGE,"E19.bottom"),sQuery(id+"F0.wireOp",EDGE,"E19.top"),sQuery(id+"F0.wireOp",EDGE,"E19.left"),sQuery(id+"F0.wireOp",EDGE,"E19.right")])],"isStart":false});
            var sketch = newSketch(context, id + "F19", { "sketchPlane" : qUnion([Q0])});
            skLineSegment(sketch, "E38.bottom", {"start": v(-36.21, 18.32) * mm, "end": v(-34.21, 18.32) * mm});
            skLineSegment(sketch, "E38.top", {"start": v(-36.21, 13.32) * mm, "end": v(-34.21, 13.32) * mm});
            skLineSegment(sketch, "E38.left", {"start": v(-36.21, 18.32) * mm, "end": v(-36.21, 13.32) * mm});
            skLineSegment(sketch, "E38.right", {"start": v(-34.21, 18.32) * mm, "end": v(-34.21, 13.32) * mm});
            skSolve(sketch);
        }
        {
            var Q0;
            Q0=makeQuery(id+"F19.imprint","IMPRINT",FACE,{"disambiguationData":[TD([[makeQuery(id+"F19.imprint","IMPRINT",EDGE,{"derivedFrom":sQuery(id+"F19.wireOp",EDGE,"E38.bottom")}),-1.0]])]});
            extrude(context, id + "F20", {"entities" : qUnion([Q0]), "operationType" : NewBodyOperationType.REMOVE, "oppositeDirection" : true, "depth" : 1 * mm});
        }
        {
            var Q0;
            Q0=makeQuery(id+"F20.boolean.opBoolean","COPY",FACE,{"derivedFrom":makeQuery(id+"F20.opExtrude","CAP_FACE",FACE,{"disambiguationData":[OSD([sQuery(id+"F19.wireOp",EDGE,"E38.bottom"),sQuery(id+"F19.wireOp",EDGE,"E38.top"),sQuery(id+"F19.wireOp",EDGE,"E38.left"),sQuery(id+"F19.wireOp",EDGE,"E38.right")])],"isStart":false})});
            var sketch = newSketch(context, id + "F21", { "sketchPlane" : qUnion([Q0])});
            skLineSegment(sketch, "E39.bottom", {"start": v(-36.21, 15.82) * mm, "end": v(-34.21, 15.82) * mm});
            skLineSegment(sketch, "E39.top", {"start": v(-36.21, 13.32) * mm, "end": v(-34.21, 13.32) * mm});
            skLineSegment(sketch, "E39.left", {"start": v(-36.21, 15.82) * mm, "end": v(-36.21, 13.32) * mm});
            skLineSegment(sketch, "E39.right", {"start": v(-34.21, 15.82) * mm, "end": v(-34.21, 13.32) * mm});
            skSolve(sketch);
        }
        {
            var Q0;
            Q0=makeQuery(id+"F21.imprint","IMPRINT",FACE,{"disambiguationData":[TD([[makeQuery(id+"F21.imprint","IMPRINT",EDGE,{"derivedFrom":sQuery(id+"F21.wireOp",EDGE,"E39.bottom")}),-1.0]])]});
            extrude(context, id + "F22", {"entities" : qUnion([Q0]), "operationType" : NewBodyOperationType.ADD, "depth" : 2 * mm});
        }
        {
            var Q0;
            Q0=makeQuery(id+"F0.imprint","IMPRINT",FACE,{"disambiguationData":[TD([[makeQuery(id+"F0.imprint","IMPRINT",EDGE,{"derivedFrom":sQuery(id+"F0.wireOp",EDGE,"E20.bottom")}),-1.0]])]});
            extrude(context, id + "F23", {"entities" : qUnion([Q0]), "depth" : 3 * mm});
        }
        {
            var Q0;
            Q0=makeQuery(id+"F23.opExtrude","CAP_FACE",FACE,{"disambiguationData":[OSD([sQuery(id+"F0.wireOp",EDGE,"E20.bottom"),sQuery(id+"F0.wireOp",EDGE,"E20.top"),sQuery(id+"F0.wireOp",EDGE,"E20.left"),sQuery(id+"F0.wireOp",EDGE,"E20.right")])],"isStart":false});
            var sketch = newSketch(context, id + "F24", { "sketchPlane" : qUnion([Q0])});
            skCircle(sketch, "E40", {"center": v(18.1, 8.97) * mm, "radius": 2 * mm});
            skLineSegment(sketch, "E41", {"start": v(18.09, 11.45) * mm, "end": v(18.09, 6.45) * mm, "construction": true});
            skSolve(sketch);
        }
        {
            var Q0;
            Q0=makeQuery(id+"F24.imprint","IMPRINT",FACE,{"disambiguationData":[TD([[makeQuery(id+"F24.imprint","IMPRINT",EDGE,{"derivedFrom":sQuery(id+"F24.wireOp",EDGE,"E40")}),1.0]])]});
            extrude(context, id + "F25", {"entities" : qUnion([Q0]), "operationType" : NewBodyOperationType.ADD, "depth" : 0.5 * mm});
        }
        {
            var Q0;
            Q0=makeQuery(id+"F23.opExtrude","CAP_FACE",FACE,{"disambiguationData":[OSD([sQuery(id+"F0.wireOp",EDGE,"E20.bottom"),sQuery(id+"F0.wireOp",EDGE,"E20.top"),sQuery(id+"F0.wireOp",EDGE,"E20.left"),sQuery(id+"F0.wireOp",EDGE,"E20.right")])],"isStart":false});
            var sketch = newSketch(context, id + "F26", { "sketchPlane" : qUnion([Q0])});
            skCircle(sketch, "E42", {"center": v(16.17, 10.87) * mm, "radius": 0.5 * mm});
            skCircle(sketch, "E43", {"center": v(19.97, 10.87) * mm, "radius": 0.5 * mm});
            skCircle(sketch, "E44", {"center": v(19.99, 7.02) * mm, "radius": 0.5 * mm});
            skCircle(sketch, "E45", {"center": v(16.19, 7.04) * mm, "radius": 0.5 * mm});
            skSolve(sketch);
        }
        {
            var Q0;
            Q0=makeQuery(id+"F26.imprint","IMPRINT",FACE,{"disambiguationData":[TD([[makeQuery(id+"F26.imprint","IMPRINT",EDGE,{"derivedFrom":sQuery(id+"F26.wireOp",EDGE,"E42")}),1.0]])]});
            var Q1;
            Q1=makeQuery(id+"F26.imprint","IMPRINT",FACE,{"disambiguationData":[TD([[makeQuery(id+"F26.imprint","IMPRINT",EDGE,{"derivedFrom":sQuery(id+"F26.wireOp",EDGE,"E45")}),1.0]])]});
            var Q2;
            Q2=makeQuery(id+"F26.imprint","IMPRINT",FACE,{"disambiguationData":[TD([[makeQuery(id+"F26.imprint","IMPRINT",EDGE,{"derivedFrom":sQuery(id+"F26.wireOp",EDGE,"E44")}),1.0]])]});
            var Q3;
            Q3=makeQuery(id+"F26.imprint","IMPRINT",FACE,{"disambiguationData":[TD([[makeQuery(id+"F26.imprint","IMPRINT",EDGE,{"derivedFrom":sQuery(id+"F26.wireOp",EDGE,"E43")}),1.0]])]});
            extrude(context, id + "F27", {"entities" : qUnion([Q0, Q1, Q2, Q3]), "operationType" : NewBodyOperationType.ADD, "depth" : 0.12 * mm});
        }
        {
            var Q0;
            {var subQ0=sQuery(id+"F0.wireOp",EDGE,"E0.left");Q0=makeQuery(id+"F1.opExtrude","SWEPT_FACE",FACE,{"disambiguationData":[OSD([subQ0]),TDD([makeQuery(id+"F0.imprint","IMPRINT",EDGE,{"disambiguationData":[TD([[makeQuery(id+"F0.imprint","INTERSECT",VERTEX,{"derivedFrom":[sQuery(id+"F0.wireOp",EDGE,"E0.top"),subQ0]}),1.0]])],"derivedFrom":subQ0})])]});}
            var sketch = newSketch(context, id + "F28", { "sketchPlane" : qUnion([Q0])});
            skLineSegment(sketch, "E46.bottom", {"start": v(2.55, 9.97) * mm, "end": v(11.55, 9.97) * mm});
            skLineSegment(sketch, "E46.top", {"start": v(2.55, -0.03) * mm, "end": v(11.55, -0.03) * mm});
            skLineSegment(sketch, "E46.left", {"start": v(2.55, 9.97) * mm, "end": v(2.55, -0.03) * mm});
            skLineSegment(sketch, "E46.right", {"start": v(11.55, 9.97) * mm, "end": v(11.55, -0.03) * mm});
            skSolve(sketch);
        }
        {
            var Q0;
            Q0 = qSketchRegion(id + "F28", true);
            extrude(context, id + "F29", {"entities" : qUnion([Q0]), "operationType" : NewBodyOperationType.ADD, "depth" : 3 * mm});
        }
        {
            var Q0;
            Q0=makeQuery(id+"F29.opExtrude","CAP_FACE",FACE,{"disambiguationData":[OSD([sQuery(id+"F28.wireOp",EDGE,"E46.bottom"),sQuery(id+"F28.wireOp",EDGE,"E46.top"),sQuery(id+"F28.wireOp",EDGE,"E46.left"),sQuery(id+"F28.wireOp",EDGE,"E46.right")])],"isStart":true});
            var sketch = newSketch(context, id + "F30", { "sketchPlane" : qUnion([Q0])});
            skArc(sketch, "E47", {"start": v(-7.05, 9.97) * mm, "mid": v(-9.89, 9) * mm, "end": v(-11.55, 6.5) * mm});
            skArc(sketch, "E48", {"start": v(-2.55, 6.5) * mm, "mid": v(-4.21, 9) * mm, "end": v(-7.05, 9.97) * mm});
            skLineSegment(sketch, "E49", {"start": v(-11.55, 6.5) * mm, "end": v(-11.55, 0) * mm});
            skLineSegment(sketch, "E50", {"start": v(-11.55, 0) * mm, "end": v(-2.55, 0) * mm});
            skLineSegment(sketch, "E51", {"start": v(-2.55, 0) * mm, "end": v(-2.55, 6.5) * mm});
            skSolve(sketch);
        }
        {
            var Q0;
            Q0 = qSketchRegion(id + "F30", true);
            extrude(context, id + "F31", {"entities" : qUnion([Q0]), "operationType" : NewBodyOperationType.ADD, "depth" : 10 * mm});
        }
        {
            var Q0;
            Q0=makeQuery(id+"F29.opExtrude","CAP_FACE",FACE,{"disambiguationData":[OSD([sQuery(id+"F28.wireOp",EDGE,"E46.bottom"),sQuery(id+"F28.wireOp",EDGE,"E46.top"),sQuery(id+"F28.wireOp",EDGE,"E46.left"),sQuery(id+"F28.wireOp",EDGE,"E46.right")])],"isStart":false});
            var sketch = newSketch(context, id + "F32", { "sketchPlane" : qUnion([Q0])});
            skCircle(sketch, "E52", {"center": v(7.05, 5.5) * mm, "radius": 3.5 * mm});
            skSolve(sketch);
        }
        {
            var Q0;
            Q0=makeQuery(id+"F32.imprint","IMPRINT",FACE,{"disambiguationData":[TD([[makeQuery(id+"F32.imprint","IMPRINT",EDGE,{"derivedFrom":sQuery(id+"F32.wireOp",EDGE,"E52")}),1.0]])]});
            extrude(context, id + "F33", {"entities" : qUnion([Q0]), "operationType" : NewBodyOperationType.REMOVE, "oppositeDirection" : true, "depth" : 10 * mm});
        }
        {
            var Q0;
            Q0=makeQuery(id+"F33.boolean.opBoolean","COPY",FACE,{"derivedFrom":makeQuery(id+"F33.opExtrude","CAP_FACE",FACE,{"disambiguationData":[OSD([sQuery(id+"F32.wireOp",EDGE,"E52")])],"isStart":false})});
            var sketch = newSketch(context, id + "F34", { "sketchPlane" : qUnion([Q0])});
            skCircle(sketch, "E53", {"center": v(7.05, 5.5) * mm, "radius": 0.5 * mm});
            skSolve(sketch);
        }
        {
            var Q0;
            Q0 = qSketchRegion(id + "F34", true);
            extrude(context, id + "F35", {"entities" : qUnion([Q0]), "operationType" : NewBodyOperationType.ADD, "depth" : 8 * mm});
        }
    });
